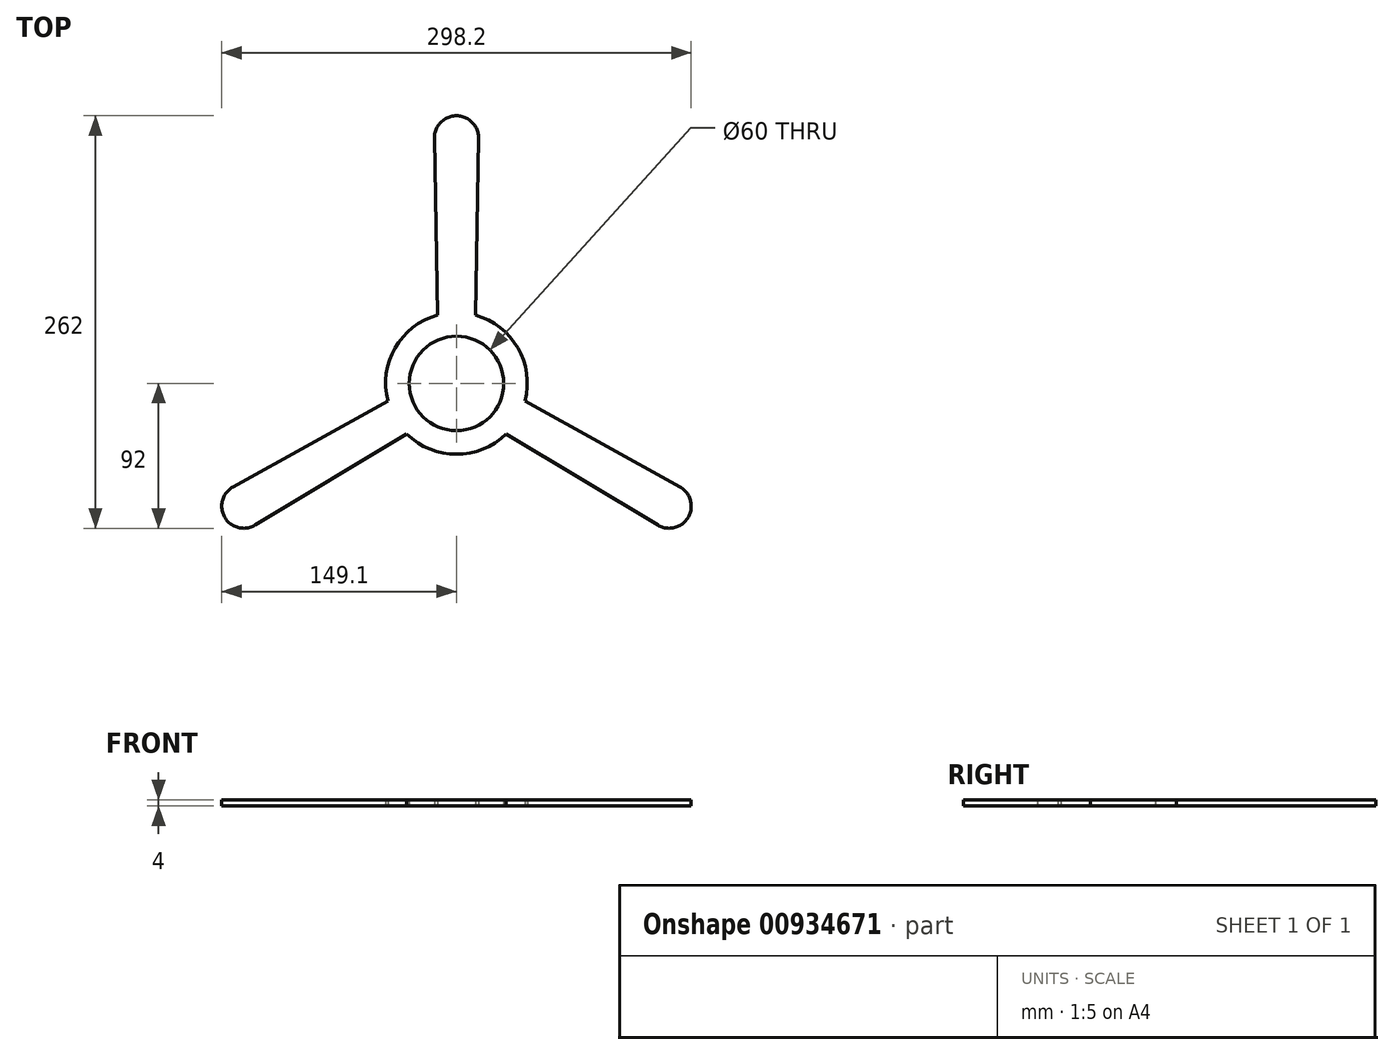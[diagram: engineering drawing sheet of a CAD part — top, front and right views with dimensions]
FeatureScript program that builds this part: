
annotation { "Feature Type Name" : "Feature", "Feature Type Description" : "" }
export const myFeature = defineFeature(function(context is Context, id is Id, definition is map)
    precondition{}
    {
        {
            var Q0;
            Q0=qCreatedBy(makeId("Top.planeOp"),FACE);
            var sketch = newSketch(context, id + "F0", { "sketchPlane" : qUnion([Q0])});
            skCircle(sketch, "E0", {"center": v(0, 0) * mm, "radius": 30 * mm});
            skArc(sketch, "E1", {"start": v(43.56, -11.3) * mm, "mid": v(38.97, 22.5) * mm, "end": v(12, 43.37) * mm});
            skLineSegment(sketch, "E2", {"start": v(0, 0) * mm, "end": v(0, 45) * mm, "construction": true});
            skLineSegment(sketch, "E3", {"start": v(-14, 155.75) * mm, "end": v(-12, 43.37) * mm});
            skLineSegment(sketch, "E4", {"start": v(14, 155.75) * mm, "end": v(12, 43.37) * mm});
            skLineSegment(sketch, "E5", {"start": v(0, 156) * mm, "end": v(0, 45) * mm, "construction": true});
            skArc(sketch, "E6", {"start": v(14, 155.75) * mm, "mid": v(0, 170) * mm, "end": v(-14, 155.75) * mm});
            skLineSegment(sketch, "E7", {"start": v(0, 0) * mm, "end": v(45, 0) * mm, "construction": true});
            skArc(sketch, "E8.1.0", {"start": v(127.88, -90) * mm, "mid": v(147.22, -85) * mm, "end": v(141.88, -65.75) * mm});
            skLineSegment(sketch, "E8.1.1", {"start": v(127.88, -90) * mm, "end": v(31.56, -32.08) * mm});
            skLineSegment(sketch, "E8.1.2", {"start": v(135.1, -78) * mm, "end": v(38.97, -22.5) * mm, "construction": true});
            skLineSegment(sketch, "E8.1.3", {"start": v(141.88, -65.75) * mm, "end": v(43.56, -11.3) * mm});
            skArc(sketch, "E8.2.0", {"start": v(-141.88, -65.75) * mm, "mid": v(-147.22, -85) * mm, "end": v(-127.88, -90) * mm});
            skLineSegment(sketch, "E8.2.1", {"start": v(-141.88, -65.75) * mm, "end": v(-43.56, -11.3) * mm});
            skLineSegment(sketch, "E8.2.2", {"start": v(-135.1, -78) * mm, "end": v(-38.97, -22.5) * mm, "construction": true});
            skLineSegment(sketch, "E8.2.3", {"start": v(-127.88, -90) * mm, "end": v(-31.56, -32.08) * mm});
            skLineSegment(sketch, "E8.anchor1", {"start": v(0, 0) * mm, "end": v(-12, 43.37) * mm, "construction": true});
            skLineSegment(sketch, "E8.anchor2", {"start": v(0, 0) * mm, "end": v(-31.56, -32.08) * mm, "construction": true});
            skArc(sketch, "E9.trimOffspring", {"start": v(-31.56, -32.08) * mm, "mid": v(0, -45) * mm, "end": v(31.56, -32.08) * mm});
            skArc(sketch, "E10.trimOffspring", {"start": v(-12, 43.37) * mm, "mid": v(-38.97, 22.5) * mm, "end": v(-43.56, -11.3) * mm});
            skSolve(sketch);
        }
        {
            var Q0;
            Q0=qSketchRegion(id+"F0",true);
            extrude(context, id + "F1", {"entities" : qUnion([Q0]), "depth" : 4 * mm, "offsetDistance" : 25 * mm});
        }
    });
